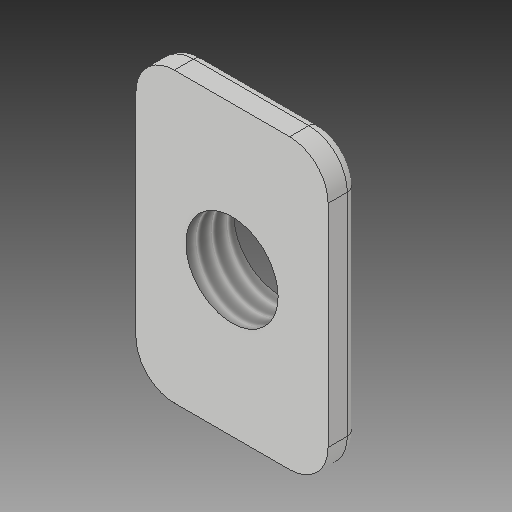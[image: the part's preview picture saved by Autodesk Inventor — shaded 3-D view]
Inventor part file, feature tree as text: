
AUTODESK INVENTOR PART (.ipt)
format: ipt  version: 2018 (Build 220112000, 112)  size: 159,232 bytes
history: native  units: mm
features: other x3, sketch x2
ambient origin geometry x8: Origin, YZ Plane, XZ Plane, XY Plane, X Axis, Y Axis, Z Axis, Center Point
bodies: Solid1 (feature_tree)
feature tree (5):
  other  "M5 Tee Nut-Generic_CPY.ipt"
  other  "Solid1::M5 Tee Nut-Generic_CPY.ipt"
  other  "TaggingFeature1"
  sketch  "Sketch1"  dims[d0=10.0mm]
  sketch  "Sketch2"
